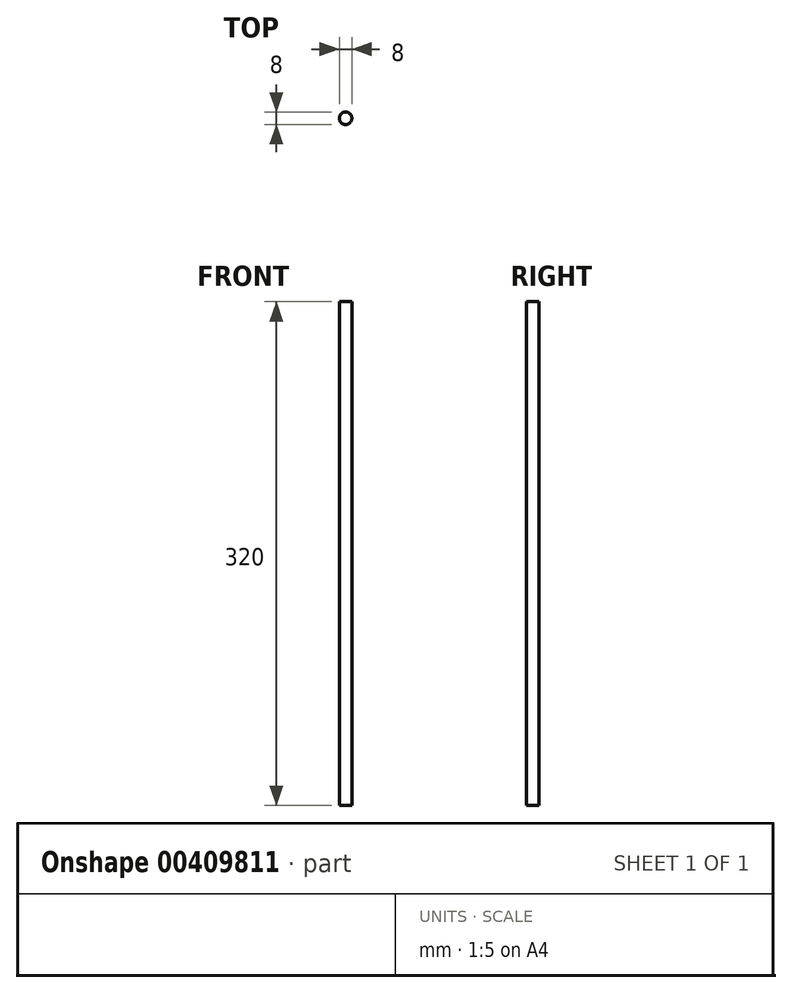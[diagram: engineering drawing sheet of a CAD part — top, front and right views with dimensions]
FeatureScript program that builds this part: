
annotation { "Feature Type Name" : "Feature", "Feature Type Description" : "" }
export const myFeature = defineFeature(function(context is Context, id is Id, definition is map)
    precondition{}
    {
        {
            var Q0;
            Q0=qCreatedBy(makeId("Top.planeOp"),FACE);
            var sketch = newSketch(context, id + "F0", { "sketchPlane" : qUnion([Q0])});
            skCircle(sketch, "E0", {"center": v(0, 0) * mm, "radius": 4 * mm});
            skSolve(sketch);
        }
        {
            var Q0;
            Q0 = qSketchRegion(id + "F0", true);
            extrude(context, id + "F1", {"entities" : qUnion([Q0]), "depth" : 320 * mm});
        }
    });
